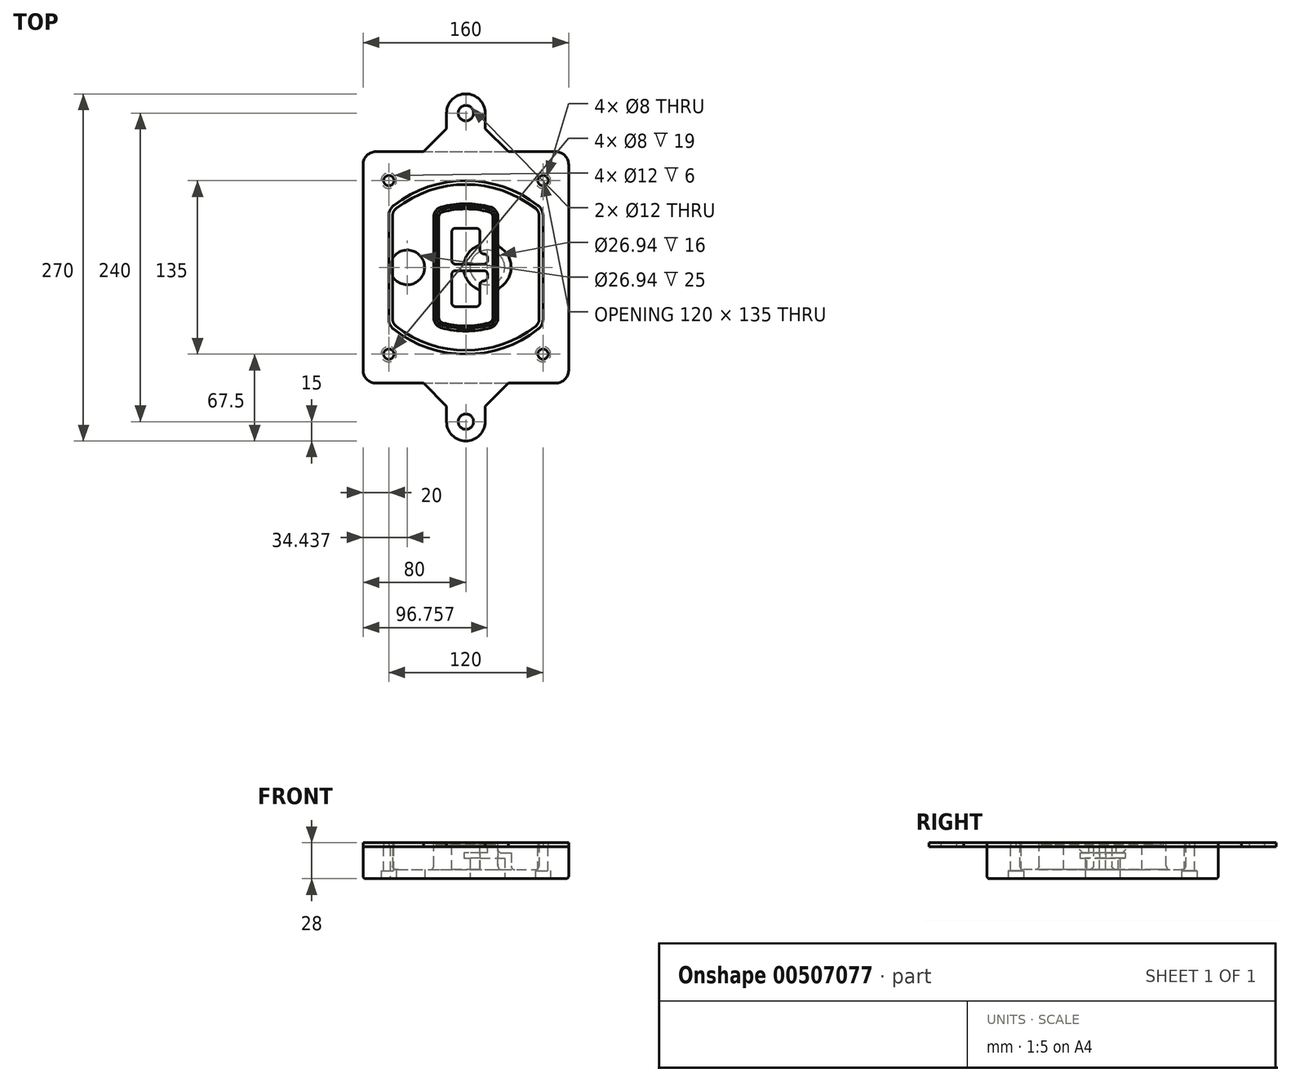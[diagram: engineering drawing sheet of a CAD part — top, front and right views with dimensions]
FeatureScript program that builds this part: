
annotation { "Feature Type Name" : "Feature", "Feature Type Description" : "" }
export const myFeature = defineFeature(function(context is Context, id is Id, definition is map)
    precondition{}
    {
        {
            var Q0;
            Q0=qCreatedBy(makeId("Top.planeOp"),FACE);
            var sketch = newSketch(context, id + "F0", { "sketchPlane" : qUnion([Q0])});
            skPoint(sketch, "E0.rect.middle", {"position": v(0, 0) * mm});
            skLineSegment(sketch, "E1.bottom", {"start": v(-70, -90) * mm, "end": v(70, -90) * mm});
            skLineSegment(sketch, "E1.top", {"start": v(-70, 90) * mm, "end": v(70, 90) * mm});
            skLineSegment(sketch, "E1.left", {"start": v(-80, -80) * mm, "end": v(-80, 80) * mm});
            skLineSegment(sketch, "E1.right", {"start": v(80, -80) * mm, "end": v(80, 80) * mm});
            skLineSegment(sketch, "E2", {"start": v(-80, 90) * mm, "end": v(80, -90) * mm, "construction": true});
            skLineSegment(sketch, "E3", {"start": v(80, 90) * mm, "end": v(-80, -90) * mm, "construction": true});
            skCircle(sketch, "E4", {"center": v(-60, 67.5) * mm, "radius": 4 * mm});
            skCircle(sketch, "E5", {"center": v(60, 67.5) * mm, "radius": 4 * mm});
            skCircle(sketch, "E6", {"center": v(60, -67.5) * mm, "radius": 4 * mm});
            skCircle(sketch, "E7", {"center": v(-60, -67.5) * mm, "radius": 4 * mm});
            skLineSegment(sketch, "E8", {"start": v(-60, 67.5) * mm, "end": v(60, 67.5) * mm, "construction": true});
            skLineSegment(sketch, "E9", {"start": v(60, 67.5) * mm, "end": v(60, -67.5) * mm, "construction": true});
            skLineSegment(sketch, "E10", {"start": v(60, -67.5) * mm, "end": v(-60, -67.5) * mm, "construction": true});
            skLineSegment(sketch, "E11", {"start": v(-60, -67.5) * mm, "end": v(-60, 67.5) * mm, "construction": true});
            skLineSegment(sketch, "E12", {"start": v(-60, 40.3) * mm, "end": v(-60, -40.3) * mm});
            skLineSegment(sketch, "E13", {"start": v(60, 40.3) * mm, "end": v(60, -40.3) * mm});
            skArc(sketch, "E14", {"start": v(56.15, 48.18) * mm, "mid": v(0, 67.5) * mm, "end": v(-56.15, 48.18) * mm});
            skArc(sketch, "E15", {"start": v(-56.15, -48.18) * mm, "mid": v(0, -67.5) * mm, "end": v(56.15, -48.18) * mm});
            skLineSegment(sketch, "E16", {"start": v(-60, 0) * mm, "end": v(60, 0) * mm, "construction": true});
            skPoint(sketch, "E17.visualSharp", {"position": v(-60, -45) * mm});
            skArc(sketch, "E17.filletArc", {"start": v(-60, -40.3) * mm, "mid": v(-58.99, -44.68) * mm, "end": v(-56.15, -48.18) * mm});
            skPoint(sketch, "E18.visualSharp", {"position": v(-60, 45) * mm});
            skArc(sketch, "E18.filletArc", {"start": v(-56.15, 48.18) * mm, "mid": v(-58.99, 44.68) * mm, "end": v(-60, 40.3) * mm});
            skPoint(sketch, "E19.visualSharp", {"position": v(60, 45) * mm});
            skArc(sketch, "E19.filletArc", {"start": v(60, 40.3) * mm, "mid": v(58.99, 44.68) * mm, "end": v(56.15, 48.18) * mm});
            skPoint(sketch, "E20.visualSharp", {"position": v(60, -45) * mm});
            skArc(sketch, "E20.filletArc", {"start": v(56.15, -48.18) * mm, "mid": v(58.99, -44.68) * mm, "end": v(60, -40.3) * mm});
            skPoint(sketch, "E21.visualSharp", {"position": v(-80, 90) * mm});
            skArc(sketch, "E21.filletArc", {"start": v(-70, 90) * mm, "mid": v(-77.07, 87.07) * mm, "end": v(-80, 80) * mm});
            skPoint(sketch, "E22.visualSharp", {"position": v(80, 90) * mm});
            skArc(sketch, "E22.filletArc", {"start": v(80, 80) * mm, "mid": v(77.07, 87.07) * mm, "end": v(70, 90) * mm});
            skPoint(sketch, "E23.visualSharp", {"position": v(80, -90) * mm});
            skArc(sketch, "E23.filletArc", {"start": v(70, -90) * mm, "mid": v(77.07, -87.07) * mm, "end": v(80, -80) * mm});
            skPoint(sketch, "E24.visualSharp", {"position": v(-80, -90) * mm});
            skArc(sketch, "E24.filletArc", {"start": v(-80, -80) * mm, "mid": v(-77.07, -87.07) * mm, "end": v(-70, -90) * mm});
            skArc(sketch, "E25.0", {"start": v(57, 40.3) * mm, "mid": v(56.3, 43.36) * mm, "end": v(54.3, 45.81) * mm});
            skLineSegment(sketch, "E25.1", {"start": v(57, 40.3) * mm, "end": v(57, -40.3) * mm});
            skArc(sketch, "E25.2", {"start": v(54.3, -45.81) * mm, "mid": v(56.3, -43.36) * mm, "end": v(57, -40.3) * mm});
            skArc(sketch, "E25.3", {"start": v(-54.3, -45.81) * mm, "mid": v(0, -64.5) * mm, "end": v(54.3, -45.81) * mm});
            skArc(sketch, "E25.4", {"start": v(-57, -40.3) * mm, "mid": v(-56.3, -43.36) * mm, "end": v(-54.3, -45.81) * mm});
            skArc(sketch, "E25.5", {"start": v(54.3, 45.81) * mm, "mid": v(0, 64.5) * mm, "end": v(-54.3, 45.81) * mm});
            skLineSegment(sketch, "E25.6", {"start": v(-57, 40.3) * mm, "end": v(-57, -40.3) * mm});
            skArc(sketch, "E25.7", {"start": v(-54.3, 45.81) * mm, "mid": v(-56.3, 43.36) * mm, "end": v(-57, 40.3) * mm});
            skArc(sketch, "E26.0", {"start": v(-58.62, 51.33) * mm, "mid": v(-62.58, 46.43) * mm, "end": v(-64, 40.3) * mm});
            skArc(sketch, "E26.1", {"start": v(58.62, 51.33) * mm, "mid": v(0, 71.5) * mm, "end": v(-58.62, 51.33) * mm});
            skArc(sketch, "E26.2", {"start": v(64, 40.3) * mm, "mid": v(62.58, 46.43) * mm, "end": v(58.62, 51.33) * mm});
            skLineSegment(sketch, "E26.3", {"start": v(64, 40.3) * mm, "end": v(64, -40.3) * mm});
            skArc(sketch, "E26.4", {"start": v(58.62, -51.33) * mm, "mid": v(62.58, -46.43) * mm, "end": v(64, -40.3) * mm});
            skLineSegment(sketch, "E26.5", {"start": v(-64, 40.3) * mm, "end": v(-64, -40.3) * mm});
            skArc(sketch, "E26.6", {"start": v(-58.62, -51.33) * mm, "mid": v(0, -71.5) * mm, "end": v(58.62, -51.33) * mm});
            skArc(sketch, "E26.7", {"start": v(-64, -40.3) * mm, "mid": v(-62.58, -46.43) * mm, "end": v(-58.62, -51.33) * mm});
            skSolve(sketch);
        }
        {
            var Q0;
            Q0=makeQuery(id+"F0.imprint","IMPRINT",FACE,{"disambiguationData":[TD([[makeQuery(id+"F0.imprint","IMPRINT",EDGE,{"derivedFrom":sQuery(id+"F0.wireOp",EDGE,"E1.bottom")}),1.0]])]});
            var Q1;
            Q1=makeQuery(id+"F0.imprint","IMPRINT",FACE,{"disambiguationData":[TD([[makeQuery(id+"F0.imprint","IMPRINT",EDGE,{"derivedFrom":sQuery(id+"F0.wireOp",EDGE,"E12")}),1.0]])]});
            var Q2;
            Q2=makeQuery(id+"F0.imprint","IMPRINT",FACE,{"disambiguationData":[TD([[makeQuery(id+"F0.imprint","IMPRINT",EDGE,{"derivedFrom":sQuery(id+"F0.wireOp",EDGE,"E25.0")}),1.0]])]});
            var Q3;
            Q3=makeQuery(id+"F0.imprint","IMPRINT",FACE,{"disambiguationData":[TD([[makeQuery(id+"F0.imprint","IMPRINT",EDGE,{"derivedFrom":sQuery(id+"F0.wireOp",EDGE,"E12")}),-1.0]])]});
            extrude(context, id + "F1", {"entities" : qUnion([Q0, Q1, Q2, Q3]), "oppositeDirection" : true, "depth" : 25 * mm});
        }
        {
            var Q0;
            Q0=makeQuery(id+"F0.imprint","IMPRINT",FACE,{"disambiguationData":[TD([[makeQuery(id+"F0.imprint","IMPRINT",EDGE,{"derivedFrom":sQuery(id+"F0.wireOp",EDGE,"E12")}),1.0]])]});
            extrude(context, id + "F2", {"entities" : qUnion([Q0]), "operationType" : NewBodyOperationType.ADD, "depth" : 3 * mm});
        }
        {
            var Q0;
            Q0=makeQuery(id+"F0.imprint","IMPRINT",FACE,{"disambiguationData":[TD([[makeQuery(id+"F0.imprint","IMPRINT",EDGE,{"derivedFrom":sQuery(id+"F0.wireOp",EDGE,"E25.0")}),1.0]])]});
            extrude(context, id + "F3", {"entities" : qUnion([Q0]), "operationType" : NewBodyOperationType.REMOVE, "oppositeDirection" : true, "depth" : 18 * mm});
        }
        {
            var Q0;
            Q0=makeQuery(id+"F2.opExtrude","CAP_FACE",FACE,{"disambiguationData":[OSD([sQuery(id+"F0.wireOp",EDGE,"E12"),sQuery(id+"F0.wireOp",EDGE,"E13"),sQuery(id+"F0.wireOp",EDGE,"E14"),sQuery(id+"F0.wireOp",EDGE,"E15"),sQuery(id+"F0.wireOp",EDGE,"E17.filletArc"),sQuery(id+"F0.wireOp",EDGE,"E18.filletArc"),sQuery(id+"F0.wireOp",EDGE,"E19.filletArc"),sQuery(id+"F0.wireOp",EDGE,"E20.filletArc"),sQuery(id+"F0.wireOp",EDGE,"E25.0"),sQuery(id+"F0.wireOp",EDGE,"E25.1"),sQuery(id+"F0.wireOp",EDGE,"E25.2"),sQuery(id+"F0.wireOp",EDGE,"E25.3"),sQuery(id+"F0.wireOp",EDGE,"E25.4"),sQuery(id+"F0.wireOp",EDGE,"E25.5"),sQuery(id+"F0.wireOp",EDGE,"E25.6"),sQuery(id+"F0.wireOp",EDGE,"E25.7")])],"isStart":false});
            var sketch = newSketch(context, id + "F4", { "sketchPlane" : qUnion([Q0])});
            skArc(sketch, "E27.0", {"start": v(-19.08, -46.97) * mm, "mid": v(0, -49.5) * mm, "end": v(19.08, -46.97) * mm});
            skArc(sketch, "E28.0", {"start": v(19.08, 46.97) * mm, "mid": v(0, 49.5) * mm, "end": v(-19.08, 46.97) * mm});
            skLineSegment(sketch, "E29", {"start": v(-25, 39.25) * mm, "end": v(-25, -39.25) * mm});
            skLineSegment(sketch, "E30", {"start": v(25, 39.25) * mm, "end": v(25, -39.25) * mm});
            skLineSegment(sketch, "E31", {"start": v(-25, 45.1) * mm, "end": v(25, 45.1) * mm, "construction": true});
            skLineSegment(sketch, "E32", {"start": v(-25, -45.1) * mm, "end": v(25, -45.1) * mm, "construction": true});
            skPoint(sketch, "E33.visualSharp", {"position": v(-25, 45.1) * mm});
            skArc(sketch, "E33.filletArc", {"start": v(-19.08, 46.97) * mm, "mid": v(-23.35, 44.11) * mm, "end": v(-25, 39.25) * mm});
            skPoint(sketch, "E34.visualSharp", {"position": v(25, 45.1) * mm});
            skArc(sketch, "E34.filletArc", {"start": v(25, 39.25) * mm, "mid": v(23.35, 44.11) * mm, "end": v(19.08, 46.97) * mm});
            skPoint(sketch, "E35.visualSharp", {"position": v(25, -45.1) * mm});
            skArc(sketch, "E35.filletArc", {"start": v(19.08, -46.97) * mm, "mid": v(23.35, -44.11) * mm, "end": v(25, -39.25) * mm});
            skPoint(sketch, "E36.visualSharp", {"position": v(-25, -45.1) * mm});
            skArc(sketch, "E36.filletArc", {"start": v(-25, -39.25) * mm, "mid": v(-23.35, -44.11) * mm, "end": v(-19.08, -46.97) * mm});
            skArc(sketch, "E37.0", {"start": v(54.3, 45.81) * mm, "mid": v(0, 64.5) * mm, "end": v(-54.3, 45.81) * mm});
            skArc(sketch, "E37.1", {"start": v(-54.3, 45.81) * mm, "mid": v(-56.3, 43.36) * mm, "end": v(-57, 40.3) * mm});
            skLineSegment(sketch, "E37.2", {"start": v(-57, 40.3) * mm, "end": v(-57, -40.3) * mm});
            skArc(sketch, "E37.3", {"start": v(-57, -40.3) * mm, "mid": v(-56.3, -43.36) * mm, "end": v(-54.3, -45.81) * mm});
            skArc(sketch, "E37.4", {"start": v(-54.3, -45.81) * mm, "mid": v(0, -64.5) * mm, "end": v(54.3, -45.81) * mm});
            skArc(sketch, "E37.5", {"start": v(54.3, -45.81) * mm, "mid": v(56.3, -43.36) * mm, "end": v(57, -40.3) * mm});
            skLineSegment(sketch, "E37.6", {"start": v(57, 40.3) * mm, "end": v(57, -40.3) * mm});
            skArc(sketch, "E37.7", {"start": v(57, 40.3) * mm, "mid": v(56.3, 43.36) * mm, "end": v(54.3, 45.81) * mm});
            skLineSegment(sketch, "E38.0", {"start": v(23, 39.25) * mm, "end": v(23, -39.25) * mm});
            skArc(sketch, "E38.1", {"start": v(18.56, -45.04) * mm, "mid": v(21.76, -42.9) * mm, "end": v(23, -39.25) * mm});
            skArc(sketch, "E38.2", {"start": v(-18.56, -45.04) * mm, "mid": v(0, -47.5) * mm, "end": v(18.56, -45.04) * mm});
            skArc(sketch, "E38.3", {"start": v(-23, -39.25) * mm, "mid": v(-21.76, -42.9) * mm, "end": v(-18.56, -45.04) * mm});
            skLineSegment(sketch, "E38.4", {"start": v(-23, 39.25) * mm, "end": v(-23, -39.25) * mm});
            skArc(sketch, "E38.5", {"start": v(23, 39.25) * mm, "mid": v(21.76, 42.9) * mm, "end": v(18.56, 45.04) * mm});
            skArc(sketch, "E38.6", {"start": v(-18.56, 45.04) * mm, "mid": v(-21.76, 42.9) * mm, "end": v(-23, 39.25) * mm});
            skArc(sketch, "E38.7", {"start": v(18.56, 45.04) * mm, "mid": v(0, 47.5) * mm, "end": v(-18.56, 45.04) * mm});
            skArc(sketch, "E39.0", {"start": v(21, 39.25) * mm, "mid": v(20.18, 41.68) * mm, "end": v(18.04, 43.1) * mm});
            skLineSegment(sketch, "E39.1", {"start": v(21, 39.25) * mm, "end": v(21, -39.25) * mm});
            skArc(sketch, "E39.2", {"start": v(18.04, -43.1) * mm, "mid": v(20.18, -41.68) * mm, "end": v(21, -39.25) * mm});
            skArc(sketch, "E39.3", {"start": v(-18.04, -43.1) * mm, "mid": v(0, -45.5) * mm, "end": v(18.04, -43.1) * mm});
            skArc(sketch, "E39.4", {"start": v(-21, -39.25) * mm, "mid": v(-20.18, -41.68) * mm, "end": v(-18.04, -43.1) * mm});
            skArc(sketch, "E39.5", {"start": v(18.04, 43.1) * mm, "mid": v(0, 45.5) * mm, "end": v(-18.04, 43.1) * mm});
            skLineSegment(sketch, "E39.6", {"start": v(-21, 39.25) * mm, "end": v(-21, -39.25) * mm});
            skArc(sketch, "E39.7", {"start": v(-18.04, 43.1) * mm, "mid": v(-20.18, 41.68) * mm, "end": v(-21, 39.25) * mm});
            skLineSegment(sketch, "E40", {"start": v(-25, 0) * mm, "end": v(25, 0) * mm, "construction": true});
            skLineSegment(sketch, "E41", {"start": v(-11, 5.5) * mm, "end": v(-11, 27.5) * mm});
            skLineSegment(sketch, "E42", {"start": v(-8, 30.5) * mm, "end": v(8, 30.5) * mm});
            skLineSegment(sketch, "E43", {"start": v(11, 27.5) * mm, "end": v(11, 13.5) * mm});
            skLineSegment(sketch, "E44", {"start": v(14, 10.5) * mm, "end": v(14, 10.5) * mm});
            skLineSegment(sketch, "E45", {"start": v(17, 7.5) * mm, "end": v(17, 5.5) * mm});
            skLineSegment(sketch, "E46", {"start": v(14, 2.5) * mm, "end": v(-8, 2.5) * mm});
            skPoint(sketch, "E47.visualSharp", {"position": v(-11, 30.5) * mm});
            skArc(sketch, "E47.filletArc", {"start": v(-8, 30.5) * mm, "mid": v(-10.12, 29.62) * mm, "end": v(-11, 27.5) * mm});
            skPoint(sketch, "E48.visualSharp", {"position": v(11, 30.5) * mm});
            skArc(sketch, "E48.filletArc", {"start": v(11, 27.5) * mm, "mid": v(10.12, 29.62) * mm, "end": v(8, 30.5) * mm});
            skPoint(sketch, "E49.visualSharp", {"position": v(11, 10.5) * mm});
            skArc(sketch, "E49.filletArc", {"start": v(11, 13.5) * mm, "mid": v(11.88, 11.38) * mm, "end": v(14, 10.5) * mm});
            skPoint(sketch, "E50.visualSharp", {"position": v(17, 10.5) * mm});
            skArc(sketch, "E50.filletArc", {"start": v(17, 7.5) * mm, "mid": v(16.12, 9.62) * mm, "end": v(14, 10.5) * mm});
            skPoint(sketch, "E51.visualSharp", {"position": v(17, 2.5) * mm});
            skArc(sketch, "E51.filletArc", {"start": v(14, 2.5) * mm, "mid": v(16.12, 3.38) * mm, "end": v(17, 5.5) * mm});
            skPoint(sketch, "E52.visualSharp", {"position": v(-11, 2.5) * mm});
            skArc(sketch, "E52.filletArc", {"start": v(-11, 5.5) * mm, "mid": v(-10.12, 3.38) * mm, "end": v(-8, 2.5) * mm});
            skLineSegment(sketch, "E53.0.MirrorCS", {"start": v(14, -2.5) * mm, "end": v(-8, -2.5) * mm});
            skArc(sketch, "E54.0.MirrorCS", {"start": v(-11, -5.5) * mm, "mid": v(-10.12, -3.38) * mm, "end": v(-8, -2.5) * mm});
            skLineSegment(sketch, "E55.0.MirrorCS", {"start": v(-11, -5.5) * mm, "end": v(-11, -27.5) * mm});
            skArc(sketch, "E56.0.MirrorCS", {"start": v(-8, -30.5) * mm, "mid": v(-10.12, -29.62) * mm, "end": v(-11, -27.5) * mm});
            skLineSegment(sketch, "E57.0.MirrorCS", {"start": v(-8, -30.5) * mm, "end": v(8, -30.5) * mm});
            skArc(sketch, "E58.0.MirrorCS", {"start": v(11, -27.5) * mm, "mid": v(10.12, -29.62) * mm, "end": v(8, -30.5) * mm});
            skLineSegment(sketch, "E59.0.MirrorCS", {"start": v(11, -27.5) * mm, "end": v(11, -13.5) * mm});
            skArc(sketch, "E60.0.MirrorCS", {"start": v(11, -13.5) * mm, "mid": v(11.88, -11.38) * mm, "end": v(14, -10.5) * mm});
            skArc(sketch, "E61.0.MirrorCS", {"start": v(17, -7.5) * mm, "mid": v(16.12, -9.62) * mm, "end": v(14, -10.5) * mm});
            skLineSegment(sketch, "E62.0.MirrorCS", {"start": v(17, -7.5) * mm, "end": v(17, -5.5) * mm});
            skArc(sketch, "E63.0.MirrorCS", {"start": v(14, -2.5) * mm, "mid": v(16.12, -3.38) * mm, "end": v(17, -5.5) * mm});
            skSolve(sketch);
        }
        {
            var Q0;
            Q0=makeQuery(id+"F4.imprint","IMPRINT",FACE,{"disambiguationData":[TD([[makeQuery(id+"F4.imprint","IMPRINT",EDGE,{"derivedFrom":sQuery(id+"F4.wireOp",EDGE,"E27.0")}),1.0]])]});
            var Q1;
            Q1=makeQuery(id+"F4.imprint","IMPRINT",FACE,{"disambiguationData":[TD([[makeQuery(id+"F4.imprint","IMPRINT",EDGE,{"derivedFrom":sQuery(id+"F4.wireOp",EDGE,"E38.0")}),-1.0]])]});
            var Q2;
            Q2=makeQuery(id+"F4.imprint","IMPRINT",FACE,{"disambiguationData":[TD([[makeQuery(id+"F4.imprint","IMPRINT",EDGE,{"derivedFrom":sQuery(id+"F4.wireOp",EDGE,"E39.0")}),1.0]])]});
            extrude(context, id + "F5", {"entities" : qUnion([Q0, Q1, Q2]), "operationType" : NewBodyOperationType.ADD, "endBound" : BoundingType.UP_TO_NEXT, "oppositeDirection" : true, "depth" : 25 * mm});
        }
        {
            var Q0;
            Q0=makeQuery(id+"F4.imprint","IMPRINT",FACE,{"disambiguationData":[TD([[makeQuery(id+"F4.imprint","IMPRINT",EDGE,{"derivedFrom":sQuery(id+"F4.wireOp",EDGE,"E38.0")}),-1.0]])]});
            extrude(context, id + "F6", {"entities" : qUnion([Q0]), "operationType" : NewBodyOperationType.REMOVE, "oppositeDirection" : true, "depth" : 2 * mm});
        }
        {
            var Q0;
            Q0=makeQuery(id+"F1.opExtrude","CAP_FACE",FACE,{"disambiguationData":[OSD([sQuery(id+"F0.wireOp",EDGE,"E1.bottom"),sQuery(id+"F0.wireOp",EDGE,"E1.top"),sQuery(id+"F0.wireOp",EDGE,"E1.left"),sQuery(id+"F0.wireOp",EDGE,"E1.right"),sQuery(id+"F0.wireOp",EDGE,"E4"),sQuery(id+"F0.wireOp",EDGE,"E5"),sQuery(id+"F0.wireOp",EDGE,"E6"),sQuery(id+"F0.wireOp",EDGE,"E7"),sQuery(id+"F0.wireOp",EDGE,"E21.filletArc"),sQuery(id+"F0.wireOp",EDGE,"E22.filletArc"),sQuery(id+"F0.wireOp",EDGE,"E23.filletArc"),sQuery(id+"F0.wireOp",EDGE,"E24.filletArc")])],"isStart":false});
            var sketch = newSketch(context, id + "F7", { "sketchPlane" : qUnion([Q0])});
            skCircle(sketch, "E64", {"center": v(16.76, 0) * mm, "radius": 13.47 * mm});
            skCircle(sketch, "E65", {"center": v(-45.56, 0) * mm, "radius": 13.47 * mm});
            skLineSegment(sketch, "E66", {"start": v(80, 0) * mm, "end": v(-80, 0) * mm});
            skCircle(sketch, "E67", {"center": v(16.76, 0) * mm, "radius": 18.47 * mm});
            skCircle(sketch, "E68", {"center": v(60, -67.5) * mm, "radius": 6 * mm});
            skCircle(sketch, "E69", {"center": v(-60, -67.5) * mm, "radius": 6 * mm});
            skCircle(sketch, "E70", {"center": v(-60, 67.5) * mm, "radius": 6 * mm});
            skCircle(sketch, "E71", {"center": v(60, 67.5) * mm, "radius": 6 * mm});
            skSolve(sketch);
        }
        {
            var Q0;
            {var subQ1=sQuery(id+"F7.wireOp",EDGE,"E66");var subQ4=sQuery(id+"F7.wireOp",EDGE,"E64");var subQ6=makeQuery(id+"F7.imprint","INTERSECT",VERTEX,{"disambiguationData":[OD(0.0)],"derivedFrom":[subQ4,subQ1]});Q0=makeQuery(id+"F7.imprint","IMPRINT",FACE,{"disambiguationData":[TD([[makeQuery(id+"F7.imprint","IMPRINT",EDGE,{"disambiguationData":[TD([[subQ6,-1.0]])],"derivedFrom":subQ4}),-1.0]])]});}
            var Q1;
            {var subQ0=sQuery(id+"F7.wireOp",EDGE,"E66");var subQ1=sQuery(id+"F7.wireOp",EDGE,"E64");var subQ3=makeQuery(id+"F7.imprint","INTERSECT",VERTEX,{"disambiguationData":[OD(0.0)],"derivedFrom":[subQ1,subQ0]});Q1=makeQuery(id+"F7.imprint","IMPRINT",FACE,{"disambiguationData":[TD([[makeQuery(id+"F7.imprint","IMPRINT",EDGE,{"disambiguationData":[TD([[subQ3,-1.0]])],"derivedFrom":subQ1}),1.0]])]});}
            var Q2;
            {var subQ0=sQuery(id+"F7.wireOp",EDGE,"E66");var subQ1=sQuery(id+"F7.wireOp",EDGE,"E64");var subQ3=makeQuery(id+"F7.imprint","INTERSECT",VERTEX,{"disambiguationData":[OD(0.0)],"derivedFrom":[subQ1,subQ0]});Q2=makeQuery(id+"F7.imprint","IMPRINT",FACE,{"disambiguationData":[TD([[makeQuery(id+"F7.imprint","IMPRINT",EDGE,{"disambiguationData":[TD([[subQ3,1.0]])],"derivedFrom":subQ1}),1.0]])]});}
            var Q3;
            {var subQ1=sQuery(id+"F7.wireOp",EDGE,"E66");var subQ4=sQuery(id+"F7.wireOp",EDGE,"E64");var subQ6=makeQuery(id+"F7.imprint","INTERSECT",VERTEX,{"disambiguationData":[OD(0.0)],"derivedFrom":[subQ4,subQ1]});Q3=makeQuery(id+"F7.imprint","IMPRINT",FACE,{"disambiguationData":[TD([[makeQuery(id+"F7.imprint","IMPRINT",EDGE,{"disambiguationData":[TD([[subQ6,1.0]])],"derivedFrom":subQ4}),-1.0]])]});}
            extrude(context, id + "F8", {"entities" : qUnion([Q0, Q1, Q2, Q3]), "operationType" : NewBodyOperationType.ADD, "oppositeDirection" : true, "depth" : 20 * mm});
        }
        {
            var Q0;
            {var subQ0=sQuery(id+"F7.wireOp",EDGE,"E66");var subQ1=sQuery(id+"F7.wireOp",EDGE,"E64");var subQ3=makeQuery(id+"F7.imprint","INTERSECT",VERTEX,{"disambiguationData":[OD(0.0)],"derivedFrom":[subQ1,subQ0]});Q0=makeQuery(id+"F7.imprint","IMPRINT",FACE,{"disambiguationData":[TD([[makeQuery(id+"F7.imprint","IMPRINT",EDGE,{"disambiguationData":[TD([[subQ3,-1.0]])],"derivedFrom":subQ1}),1.0]])]});}
            var Q1;
            {var subQ0=sQuery(id+"F7.wireOp",EDGE,"E66");var subQ1=sQuery(id+"F7.wireOp",EDGE,"E64");var subQ3=makeQuery(id+"F7.imprint","INTERSECT",VERTEX,{"disambiguationData":[OD(0.0)],"derivedFrom":[subQ1,subQ0]});Q1=makeQuery(id+"F7.imprint","IMPRINT",FACE,{"disambiguationData":[TD([[makeQuery(id+"F7.imprint","IMPRINT",EDGE,{"disambiguationData":[TD([[subQ3,1.0]])],"derivedFrom":subQ1}),1.0]])]});}
            extrude(context, id + "F9", {"entities" : qUnion([Q0, Q1]), "operationType" : NewBodyOperationType.REMOVE, "oppositeDirection" : true, "depth" : 16 * mm});
        }
        {
            var Q0;
            {var subQ0=sQuery(id+"F7.wireOp",EDGE,"E66");var subQ1=sQuery(id+"F7.wireOp",EDGE,"E65");var subQ3=makeQuery(id+"F7.imprint","INTERSECT",VERTEX,{"disambiguationData":[OD(0.0)],"derivedFrom":[subQ1,subQ0]});Q0=makeQuery(id+"F7.imprint","IMPRINT",FACE,{"disambiguationData":[TD([[makeQuery(id+"F7.imprint","IMPRINT",EDGE,{"disambiguationData":[TD([[subQ3,-1.0]])],"derivedFrom":subQ1}),1.0]])]});}
            var Q1;
            {var subQ0=sQuery(id+"F7.wireOp",EDGE,"E66");var subQ1=sQuery(id+"F7.wireOp",EDGE,"E65");var subQ3=makeQuery(id+"F7.imprint","INTERSECT",VERTEX,{"disambiguationData":[OD(0.0)],"derivedFrom":[subQ1,subQ0]});Q1=makeQuery(id+"F7.imprint","IMPRINT",FACE,{"disambiguationData":[TD([[makeQuery(id+"F7.imprint","IMPRINT",EDGE,{"disambiguationData":[TD([[subQ3,1.0]])],"derivedFrom":subQ1}),1.0]])]});}
            extrude(context, id + "F10", {"entities" : qUnion([Q0, Q1]), "operationType" : NewBodyOperationType.REMOVE, "oppositeDirection" : true, "depth" : 25 * mm});
        }
        {
            var Q0;
            Q0=makeQuery(id+"F7.imprint","IMPRINT",FACE,{"disambiguationData":[TD([[makeQuery(id+"F7.imprint","IMPRINT",EDGE,{"derivedFrom":sQuery(id+"F7.wireOp",EDGE,"E68")}),1.0]])]});
            var Q1;
            Q1=makeQuery(id+"F7.imprint","IMPRINT",FACE,{"disambiguationData":[TD([[makeQuery(id+"F7.imprint","IMPRINT",EDGE,{"derivedFrom":makeQuery(id+"F1.opExtrude","CAP_EDGE",EDGE,{"disambiguationData":[OSD([sQuery(id+"F0.wireOp",EDGE,"E5")])],"isStart":false})}),-1.0]])]});
            var Q2;
            Q2=makeQuery(id+"F7.imprint","IMPRINT",FACE,{"disambiguationData":[TD([[makeQuery(id+"F7.imprint","IMPRINT",EDGE,{"derivedFrom":sQuery(id+"F7.wireOp",EDGE,"E69")}),1.0]])]});
            var Q3;
            Q3=makeQuery(id+"F7.imprint","IMPRINT",FACE,{"disambiguationData":[TD([[makeQuery(id+"F7.imprint","IMPRINT",EDGE,{"derivedFrom":makeQuery(id+"F1.opExtrude","CAP_EDGE",EDGE,{"disambiguationData":[OSD([sQuery(id+"F0.wireOp",EDGE,"E4")])],"isStart":false})}),-1.0]])]});
            var Q4;
            Q4=makeQuery(id+"F7.imprint","IMPRINT",FACE,{"disambiguationData":[TD([[makeQuery(id+"F7.imprint","IMPRINT",EDGE,{"derivedFrom":sQuery(id+"F7.wireOp",EDGE,"E70")}),1.0]])]});
            var Q5;
            Q5=makeQuery(id+"F7.imprint","IMPRINT",FACE,{"disambiguationData":[TD([[makeQuery(id+"F7.imprint","IMPRINT",EDGE,{"derivedFrom":makeQuery(id+"F1.opExtrude","CAP_EDGE",EDGE,{"disambiguationData":[OSD([sQuery(id+"F0.wireOp",EDGE,"E7")])],"isStart":false})}),-1.0]])]});
            var Q6;
            Q6=makeQuery(id+"F7.imprint","IMPRINT",FACE,{"disambiguationData":[TD([[makeQuery(id+"F7.imprint","IMPRINT",EDGE,{"derivedFrom":sQuery(id+"F7.wireOp",EDGE,"E71")}),1.0]])]});
            var Q7;
            Q7=makeQuery(id+"F7.imprint","IMPRINT",FACE,{"disambiguationData":[TD([[makeQuery(id+"F7.imprint","IMPRINT",EDGE,{"derivedFrom":makeQuery(id+"F1.opExtrude","CAP_EDGE",EDGE,{"disambiguationData":[OSD([sQuery(id+"F0.wireOp",EDGE,"E6")])],"isStart":false})}),-1.0]])]});
            extrude(context, id + "F11", {"entities" : qUnion([Q0, Q1, Q2, Q3, Q4, Q5, Q6, Q7]), "operationType" : NewBodyOperationType.REMOVE, "oppositeDirection" : true, "depth" : 6 * mm});
        }
        {
            var Q0;
            Q0=makeQuery(id+"F9.boolean.opBoolean","COPY",FACE,{"derivedFrom":makeQuery(id+"F9.opExtrude","CAP_FACE",FACE,{"disambiguationData":[OSD([sQuery(id+"F7.wireOp",EDGE,"E64")])],"isStart":false})});
            var sketch = newSketch(context, id + "F12", { "sketchPlane" : qUnion([Q0])});
            skArc(sketch, "E72.0", {"start": v(11, 17.55) * mm, "mid": v(2.57, 11.82) * mm, "end": v(-1.54, 2.5) * mm});
            skArc(sketch, "E72.1", {"start": v(-1.54, -2.5) * mm, "mid": v(2.57, -11.82) * mm, "end": v(11, -17.55) * mm});
            skLineSegment(sketch, "E73", {"start": v(-1.54, -2.5) * mm, "end": v(14, -2.5) * mm});
            skLineSegment(sketch, "E74.0", {"start": v(14, 2.5) * mm, "end": v(-1.54, 2.5) * mm});
            skArc(sketch, "E74.1", {"start": v(14, 2.5) * mm, "mid": v(16.12, 3.38) * mm, "end": v(17, 5.5) * mm});
            skLineSegment(sketch, "E74.2", {"start": v(17, 7.5) * mm, "end": v(17, 5.5) * mm});
            skArc(sketch, "E74.3", {"start": v(17, 7.5) * mm, "mid": v(16.12, 9.62) * mm, "end": v(14, 10.5) * mm});
            skArc(sketch, "E74.4", {"start": v(11, 13.5) * mm, "mid": v(11.88, 11.38) * mm, "end": v(14, 10.5) * mm});
            skLineSegment(sketch, "E74.5", {"start": v(11, 17.55) * mm, "end": v(11, 13.5) * mm});
            skLineSegment(sketch, "E74.7", {"start": v(14, -2.5) * mm, "end": v(-1.54, -2.5) * mm});
            skArc(sketch, "E74.8", {"start": v(14, -2.5) * mm, "mid": v(16.12, -3.38) * mm, "end": v(17, -5.5) * mm});
            skLineSegment(sketch, "E74.9", {"start": v(17, -7.5) * mm, "end": v(17, -5.5) * mm});
            skArc(sketch, "E74.10", {"start": v(17, -7.5) * mm, "mid": v(16.12, -9.62) * mm, "end": v(14, -10.5) * mm});
            skArc(sketch, "E74.11", {"start": v(11, -13.5) * mm, "mid": v(11.88, -11.38) * mm, "end": v(14, -10.5) * mm});
            skLineSegment(sketch, "E74.12", {"start": v(11, -17.55) * mm, "end": v(11, -13.5) * mm});
            skPoint(sketch, "E75.orphan", {"position": v(11, -27.5) * mm});
            skPoint(sketch, "E76.orphan", {"position": v(-8, -2.5) * mm});
            skPoint(sketch, "E77.orphan", {"position": v(-8, 2.5) * mm});
            skPoint(sketch, "E78.orphan", {"position": v(11, 27.5) * mm});
            skSolve(sketch);
        }
        {
            var Q0;
            {var subQ7=sQuery(id+"F12.wireOp",EDGE,"E72.0");var subQ14=sQuery(id+"F12.wireOp",EDGE,"E72.1");var subQ16=sQuery(id+"F12.wireOp",EDGE,"E74.1");var subQ18=sQuery(id+"F12.wireOp",EDGE,"E74.8");Q0=qUnion([makeQuery(id+"F12.imprint","IMPRINT",FACE,{"disambiguationData":[TD([[makeQuery(id+"F12.imprint","IMPRINT",EDGE,{"derivedFrom":subQ7}),1.0]])]}),makeQuery(id+"F12.imprint","IMPRINT",FACE,{"disambiguationData":[TD([[makeQuery(id+"F12.imprint","IMPRINT",EDGE,{"derivedFrom":subQ14}),1.0]])]}),makeQuery(id+"F12.imprint","IMPRINT",FACE,{"disambiguationData":[TD([[makeQuery(id+"F12.imprint","IMPRINT",EDGE,{"derivedFrom":subQ16}),1.0]])]}),makeQuery(id+"F12.imprint","IMPRINT",FACE,{"disambiguationData":[TD([[makeQuery(id+"F12.imprint","IMPRINT",EDGE,{"derivedFrom":subQ18}),-1.0]])]})]);}
            var Q1;
            Q1=makeQuery(id+"F5.boolean.opBoolean","SPLIT",FACE,{"disambiguationData":[TD([makeQuery(id+"F5.opExtrude","SWEPT_FACE",FACE,{"disambiguationData":[OSD([sQuery(id+"F4.wireOp",EDGE,"E41")])]})])],"derivedFrom":makeQuery(id+"F3.boolean.opBoolean","COPY",FACE,{"derivedFrom":makeQuery(id+"F3.opExtrude","CAP_FACE",FACE,{"disambiguationData":[OSD([sQuery(id+"F0.wireOp",EDGE,"E25.0"),sQuery(id+"F0.wireOp",EDGE,"E25.1"),sQuery(id+"F0.wireOp",EDGE,"E25.2"),sQuery(id+"F0.wireOp",EDGE,"E25.3"),sQuery(id+"F0.wireOp",EDGE,"E25.4"),sQuery(id+"F0.wireOp",EDGE,"E25.5"),sQuery(id+"F0.wireOp",EDGE,"E25.6"),sQuery(id+"F0.wireOp",EDGE,"E25.7")])],"isStart":false})})});
            extrude(context, id + "F13", {"entities" : qUnion([Q0]), "operationType" : NewBodyOperationType.REMOVE, "endBound" : BoundingType.UP_TO_SURFACE, "endBoundEntityFace" : qUnion([Q1]), "depth" : 25 * mm});
        }
        {
            var Q0;
            Q0=makeQuery(id+"F3.boolean.opBoolean","COPY",EDGE,{"derivedFrom":makeQuery(id+"F3.opExtrude","CAP_EDGE",EDGE,{"disambiguationData":[OSD([sQuery(id+"F0.wireOp",EDGE,"E25.6")])],"isStart":false})});
            var Q1;
            Q1=makeQuery(id+"F8.boolean.opBoolean","INTERSECT",EDGE,{"derivedFrom":[makeQuery(id+"F5.opExtrude","SWEPT_FACE",FACE,{"disambiguationData":[OSD([sQuery(id+"F4.wireOp",EDGE,"E30")])]}),makeQuery(id+"F8.opExtrude","CAP_FACE",FACE,{"disambiguationData":[OSD([sQuery(id+"F7.wireOp",EDGE,"E67")])],"isStart":false})]});
            var Q2;
            Q2=makeQuery(id+"F8.boolean.opBoolean","INTERSECT",EDGE,{"disambiguationData":[OD(1.0)],"derivedFrom":[makeQuery(id+"F5.opExtrude","SWEPT_FACE",FACE,{"disambiguationData":[OSD([sQuery(id+"F4.wireOp",EDGE,"E30")])]}),makeQuery(id+"F8.opExtrude","SWEPT_FACE",FACE,{"disambiguationData":[OSD([sQuery(id+"F7.wireOp",EDGE,"E67")])]})]});
            var Q3;
            {var subQ0=sQuery(id+"F4.wireOp",EDGE,"E30");Q3=makeQuery(id+"F8.boolean.opBoolean","SPLIT",EDGE,{"disambiguationData":[TD([makeQuery(id+"F5.opExtrude","SWEPT_FACE",FACE,{"disambiguationData":[OSD([sQuery(id+"F4.wireOp",EDGE,"E35.filletArc")])]})])],"derivedFrom":makeQuery(id+"F5.opExtrude","CAP_EDGE",EDGE,{"disambiguationData":[OSD([subQ0])],"isStart":false})});}
            var Q4;
            {var subQ0=sQuery(id+"F0.wireOp",EDGE,"E25.7");var subQ1=sQuery(id+"F0.wireOp",EDGE,"E25.1");var subQ2=sQuery(id+"F0.wireOp",EDGE,"E25.6");var subQ3=sQuery(id+"F0.wireOp",EDGE,"E25.5");var subQ4=sQuery(id+"F0.wireOp",EDGE,"E25.4");var subQ5=sQuery(id+"F0.wireOp",EDGE,"E25.0");var subQ6=sQuery(id+"F0.wireOp",EDGE,"E25.2");var subQ7=sQuery(id+"F0.wireOp",EDGE,"E25.3");Q4=makeQuery(id+"F8.boolean.opBoolean","INTERSECT",EDGE,{"derivedFrom":[makeQuery(id+"F5.boolean.opBoolean","SPLIT",FACE,{"disambiguationData":[TD([makeQuery(id+"F2.opExtrude","SWEPT_FACE",FACE,{"disambiguationData":[OSD([subQ5])]})])],"derivedFrom":makeQuery(id+"F3.boolean.opBoolean","COPY",FACE,{"derivedFrom":makeQuery(id+"F3.opExtrude","CAP_FACE",FACE,{"disambiguationData":[OSD([subQ5,subQ1,subQ6,subQ7,subQ4,subQ3,subQ2,subQ0])],"isStart":false})})}),makeQuery(id+"F8.opExtrude","SWEPT_FACE",FACE,{"disambiguationData":[OSD([sQuery(id+"F7.wireOp",EDGE,"E67")])]})]});}
            var Q5;
            Q5=makeQuery(id+"F8.boolean.opBoolean","INTERSECT",EDGE,{"disambiguationData":[OD(0.0)],"derivedFrom":[makeQuery(id+"F5.opExtrude","SWEPT_FACE",FACE,{"disambiguationData":[OSD([sQuery(id+"F4.wireOp",EDGE,"E30")])]}),makeQuery(id+"F8.opExtrude","SWEPT_FACE",FACE,{"disambiguationData":[OSD([sQuery(id+"F7.wireOp",EDGE,"E67")])]})]});
            fillet(context, id + "F14", {"entities" : qUnion([Q0, Q1, Q2, Q3, Q4, Q5]), "radius" : 3 * mm, "tangentPropagation" : true, "allowEdgeOverflow" : false});
        }
        {
            var Q0;
            Q0=makeQuery(id+"F1.opExtrude","CAP_EDGE",EDGE,{"disambiguationData":[OSD([sQuery(id+"F0.wireOp",EDGE,"E1.bottom")])],"isStart":false});
            fillet(context, id + "F15", {"entities" : qUnion([Q0]), "radius" : 2 * mm, "tangentPropagation" : true, "allowEdgeOverflow" : false});
        }
        {
            var Q0;
            {var subQ0=sQuery(id+"F0.wireOp",EDGE,"E21.filletArc");var subQ1=sQuery(id+"F0.wireOp",EDGE,"E7");var subQ2=sQuery(id+"F0.wireOp",EDGE,"E6");var subQ3=sQuery(id+"F0.wireOp",EDGE,"E5");var subQ4=sQuery(id+"F0.wireOp",EDGE,"E4");var subQ5=sQuery(id+"F0.wireOp",EDGE,"E22.filletArc");var subQ6=sQuery(id+"F0.wireOp",EDGE,"E1.bottom");var subQ7=sQuery(id+"F0.wireOp",EDGE,"E1.right");var subQ8=sQuery(id+"F0.wireOp",EDGE,"E1.top");var subQ9=sQuery(id+"F0.wireOp",EDGE,"E1.left");var subQ10=sQuery(id+"F0.wireOp",EDGE,"E23.filletArc");var subQ11=sQuery(id+"F0.wireOp",EDGE,"E24.filletArc");Q0=makeQuery(id+"F2.boolean.opBoolean","SPLIT",FACE,{"disambiguationData":[TD([makeQuery(id+"F1.opExtrude","SWEPT_FACE",FACE,{"disambiguationData":[OSD([subQ6])]})])],"derivedFrom":makeQuery(id+"F1.opExtrude","CAP_FACE",FACE,{"disambiguationData":[OSD([subQ6,subQ8,subQ9,subQ7,subQ4,subQ3,subQ2,subQ1,subQ0,subQ5,subQ10,subQ11])],"isStart":true})});}
            var sketch = newSketch(context, id + "F16", { "sketchPlane" : qUnion([Q0])});
            skLineSegment(sketch, "E79.0", {"start": v(-70, 90) * mm, "end": v(70, 90) * mm});
            skArc(sketch, "E79.1", {"start": v(-70, 90) * mm, "mid": v(-77.07, 87.07) * mm, "end": v(-80, 80) * mm});
            skLineSegment(sketch, "E79.2", {"start": v(-80, -80) * mm, "end": v(-80, 80) * mm});
            skArc(sketch, "E79.3", {"start": v(-80, -80) * mm, "mid": v(-77.07, -87.07) * mm, "end": v(-70, -90) * mm});
            skLineSegment(sketch, "E79.4", {"start": v(-70, -90) * mm, "end": v(70, -90) * mm});
            skArc(sketch, "E79.5", {"start": v(70, -90) * mm, "mid": v(77.07, -87.07) * mm, "end": v(80, -80) * mm});
            skLineSegment(sketch, "E79.6", {"start": v(80, -80) * mm, "end": v(80, 80) * mm});
            skArc(sketch, "E79.7", {"start": v(80, 80) * mm, "mid": v(77.07, 87.07) * mm, "end": v(70, 90) * mm});
            skCircle(sketch, "E79.8", {"center": v(60, 67.5) * mm, "radius": 4 * mm});
            skCircle(sketch, "E79.9", {"center": v(-60, 67.5) * mm, "radius": 4 * mm});
            skCircle(sketch, "E79.10", {"center": v(-60, -67.5) * mm, "radius": 4 * mm});
            skCircle(sketch, "E79.11", {"center": v(60, -67.5) * mm, "radius": 4 * mm});
            skLineSegment(sketch, "E79.12", {"start": v(60, 40.3) * mm, "end": v(60, -40.3) * mm});
            skArc(sketch, "E79.13", {"start": v(56.15, -48.18) * mm, "mid": v(58.99, -44.68) * mm, "end": v(60, -40.3) * mm});
            skArc(sketch, "E79.14", {"start": v(-56.15, -48.18) * mm, "mid": v(0, -67.5) * mm, "end": v(56.15, -48.18) * mm});
            skLineSegment(sketch, "E79.15", {"start": v(-60, 40.3) * mm, "end": v(-60, -40.3) * mm});
            skArc(sketch, "E79.16", {"start": v(-56.15, 48.18) * mm, "mid": v(-58.99, 44.68) * mm, "end": v(-60, 40.3) * mm});
            skArc(sketch, "E79.17", {"start": v(56.15, 48.18) * mm, "mid": v(0, 67.5) * mm, "end": v(-56.15, 48.18) * mm});
            skArc(sketch, "E79.18", {"start": v(60, 40.3) * mm, "mid": v(58.99, 44.68) * mm, "end": v(56.15, 48.18) * mm});
            skArc(sketch, "E79.19", {"start": v(-60, -40.3) * mm, "mid": v(-58.99, -44.68) * mm, "end": v(-56.15, -48.18) * mm});
            skLineSegment(sketch, "E80", {"start": v(15, 108) * mm, "end": v(15, 120) * mm});
            skArc(sketch, "E81", {"start": v(15, 120) * mm, "mid": v(0, 135) * mm, "end": v(-15, 120) * mm});
            skCircle(sketch, "E82", {"center": v(0, 120) * mm, "radius": 6 * mm});
            skLineSegment(sketch, "E83", {"start": v(0, 120) * mm, "end": v(0, 90) * mm, "construction": true});
            skLineSegment(sketch, "E84", {"start": v(-15, 120) * mm, "end": v(-15, 108) * mm});
            skLineSegment(sketch, "E85", {"start": v(-15, 108) * mm, "end": v(-33, 90) * mm});
            skLineSegment(sketch, "E86", {"start": v(15, 108) * mm, "end": v(33, 90) * mm});
            skLineSegment(sketch, "E87", {"start": v(0, 0) * mm, "end": v(-115.2, 0) * mm, "construction": true});
            skLineSegment(sketch, "E88", {"start": v(0, 0) * mm, "end": v(94.69, 0) * mm, "construction": true});
            skLineSegment(sketch, "E89.MirrorCS", {"start": v(-15, -108) * mm, "end": v(-33, -90) * mm});
            skLineSegment(sketch, "E90.MirrorCS", {"start": v(-15, -120) * mm, "end": v(-15, -108) * mm});
            skArc(sketch, "E91.MirrorCS", {"start": v(15, -120) * mm, "mid": v(0, -135) * mm, "end": v(-15, -120) * mm});
            skCircle(sketch, "E92.MirrorC", {"center": v(0, -120) * mm, "radius": 6 * mm});
            skLineSegment(sketch, "E93.MirrorCS", {"start": v(15, -108) * mm, "end": v(15, -120) * mm});
            skLineSegment(sketch, "E94.MirrorCS", {"start": v(15, -108) * mm, "end": v(33, -90) * mm});
            skLineSegment(sketch, "E95.MirrorCS", {"start": v(0, -120) * mm, "end": v(0, -90) * mm, "construction": true});
            skSolve(sketch);
        }
        {
            var Q0;
            Q0 = qSketchRegion(id + "F16", true);
            var Q1;
            Q1=makeQuery(id+"F2.opExtrude","CAP_FACE",FACE,{"disambiguationData":[OSD([sQuery(id+"F0.wireOp",EDGE,"E12"),sQuery(id+"F0.wireOp",EDGE,"E13"),sQuery(id+"F0.wireOp",EDGE,"E14"),sQuery(id+"F0.wireOp",EDGE,"E15"),sQuery(id+"F0.wireOp",EDGE,"E17.filletArc"),sQuery(id+"F0.wireOp",EDGE,"E18.filletArc"),sQuery(id+"F0.wireOp",EDGE,"E19.filletArc"),sQuery(id+"F0.wireOp",EDGE,"E20.filletArc"),sQuery(id+"F0.wireOp",EDGE,"E25.0"),sQuery(id+"F0.wireOp",EDGE,"E25.1"),sQuery(id+"F0.wireOp",EDGE,"E25.2"),sQuery(id+"F0.wireOp",EDGE,"E25.3"),sQuery(id+"F0.wireOp",EDGE,"E25.4"),sQuery(id+"F0.wireOp",EDGE,"E25.5"),sQuery(id+"F0.wireOp",EDGE,"E25.6"),sQuery(id+"F0.wireOp",EDGE,"E25.7")])],"isStart":false});
            extrude(context, id + "F17", {"entities" : qUnion([Q0]), "endBound" : BoundingType.UP_TO_SURFACE, "endBoundEntityFace" : qUnion([Q1]), "depth" : 25 * mm});
        }
    });
